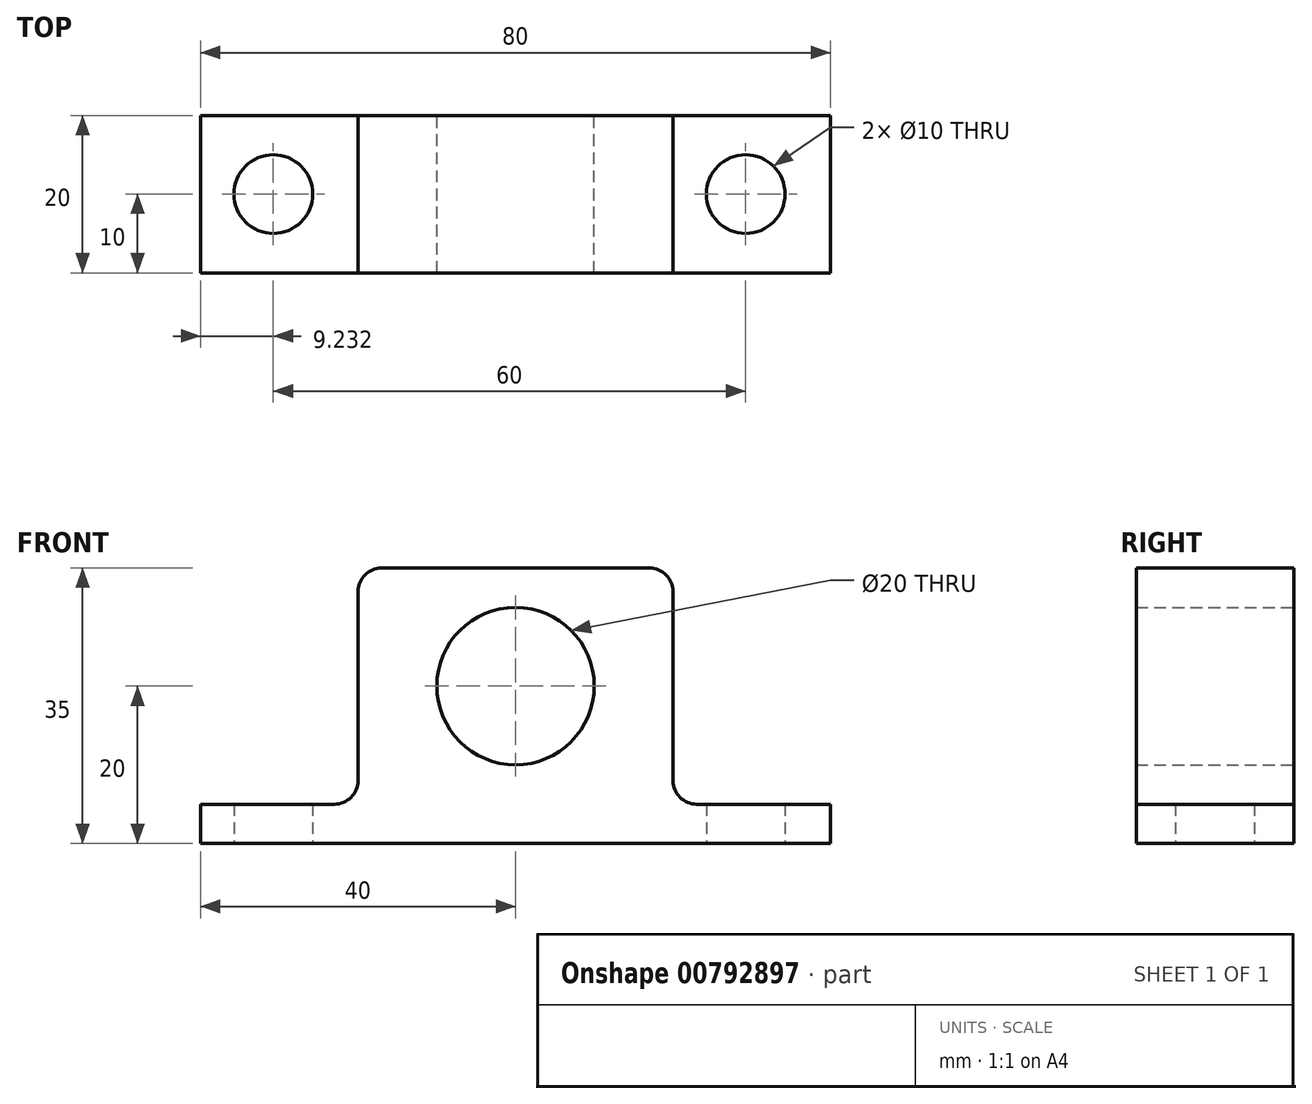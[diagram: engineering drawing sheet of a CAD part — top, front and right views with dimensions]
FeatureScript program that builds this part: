
annotation { "Feature Type Name" : "Feature", "Feature Type Description" : "" }
export const myFeature = defineFeature(function(context is Context, id is Id, definition is map)
    precondition{}
    {
        {
            var Q0;
            Q0=qCreatedBy(makeId("Front.planeOp"),FACE);
            var sketch = newSketch(context, id + "F0", { "sketchPlane" : qUnion([Q0])});
            skLineSegment(sketch, "E0", {"start": v(-40, 0) * mm, "end": v(40, 0) * mm});
            skLineSegment(sketch, "E1", {"start": v(40, 0) * mm, "end": v(40, 5) * mm});
            skLineSegment(sketch, "E2", {"start": v(40, 5) * mm, "end": v(20, 5) * mm});
            skLineSegment(sketch, "E3", {"start": v(20, 5) * mm, "end": v(20, 35) * mm});
            skLineSegment(sketch, "E4", {"start": v(20, 35) * mm, "end": v(-20, 35) * mm});
            skLineSegment(sketch, "E5", {"start": v(-20, 35) * mm, "end": v(-20, 5) * mm});
            skLineSegment(sketch, "E6", {"start": v(-20, 5) * mm, "end": v(-40, 5) * mm});
            skLineSegment(sketch, "E7", {"start": v(-40, 5) * mm, "end": v(-40, 0) * mm});
            skCircle(sketch, "E8", {"center": v(0, 20) * mm, "radius": 10 * mm});
            skSolve(sketch);
        }
        {
            var Q0;
            Q0=makeQuery(id+"F0.imprint","IMPRINT",FACE,{"disambiguationData":[TD([[makeQuery(id+"F0.imprint","IMPRINT",EDGE,{"derivedFrom":sQuery(id+"F0.wireOp",EDGE,"E0")}),1.0]])]});
            extrude(context, id + "F1", {"entities" : qUnion([Q0]), "depth" : 20 * mm, "offsetDistance" : 25 * mm});
        }
        {
            var Q0;
            Q0=makeQuery(id+"F1.opExtrude","SWEPT_EDGE",EDGE,{"disambiguationData":[OSD([sQuery(id+"F0.wireOp",EDGE,"E3"),sQuery(id+"F0.wireOp",EDGE,"E4")])]});
            var Q1;
            Q1=makeQuery(id+"F1.opExtrude","SWEPT_EDGE",EDGE,{"disambiguationData":[OSD([sQuery(id+"F0.wireOp",EDGE,"E2"),sQuery(id+"F0.wireOp",EDGE,"E3")])]});
            var Q2;
            Q2=makeQuery(id+"F1.opExtrude","SWEPT_EDGE",EDGE,{"disambiguationData":[OSD([sQuery(id+"F0.wireOp",EDGE,"E4"),sQuery(id+"F0.wireOp",EDGE,"E5")])]});
            var Q3;
            Q3=makeQuery(id+"F1.opExtrude","SWEPT_EDGE",EDGE,{"disambiguationData":[OSD([sQuery(id+"F0.wireOp",EDGE,"E5"),sQuery(id+"F0.wireOp",EDGE,"E6")])]});
            fillet(context, id + "F2", {"entities" : qUnion([Q0, Q1, Q2, Q3]), "radius" : 3 * mm, "tangentPropagation" : true, "allowEdgeOverflow" : false});
        }
        {
            var Q0;
            Q0=makeQuery(id+"F1.opExtrude","SWEPT_FACE",FACE,{"disambiguationData":[OSD([sQuery(id+"F0.wireOp",EDGE,"E0")])]});
            var sketch = newSketch(context, id + "F3", { "sketchPlane" : qUnion([Q0])});
            skPoint(sketch, "E9", {"position": v(-30.77, 10) * mm});
            skPoint(sketch, "E10", {"position": v(29.23, 10) * mm});
            skSolve(sketch);
        }
        {
            var Q0;
            Q0=sQuery(id+"F3.wireOp",VERTEX,"E9");
            var Q1;
            Q1=sQuery(id+"F3.wireOp",VERTEX,"E10");
            var Q2;
            Q2=makeQuery(id+"F1.opExtrude","SWEPT_BODY",BODY,{"disambiguationData":[OSD([sQuery(id+"F0.wireOp",EDGE,"E0"),sQuery(id+"F0.wireOp",EDGE,"E1"),sQuery(id+"F0.wireOp",EDGE,"E2"),sQuery(id+"F0.wireOp",EDGE,"E3"),sQuery(id+"F0.wireOp",EDGE,"E4"),sQuery(id+"F0.wireOp",EDGE,"E5"),sQuery(id+"F0.wireOp",EDGE,"E6"),sQuery(id+"F0.wireOp",EDGE,"E7"),sQuery(id+"F0.wireOp",EDGE,"E8")])]});
            hole(context, id + "F4", {"style" : HoleStyle.SIMPLE, "endStyle" : HoleEndStyle.THROUGH, "holeDiameter" : 10 * mm, "majorDiameter" : 5 * mm, "isTappedThrough" : true, "tappedDepth" : 12 * mm, "tapClearance" : 3, "locations" : qUnion([Q0, Q1]), "scope" : qUnion([Q2])});
        }
    });
